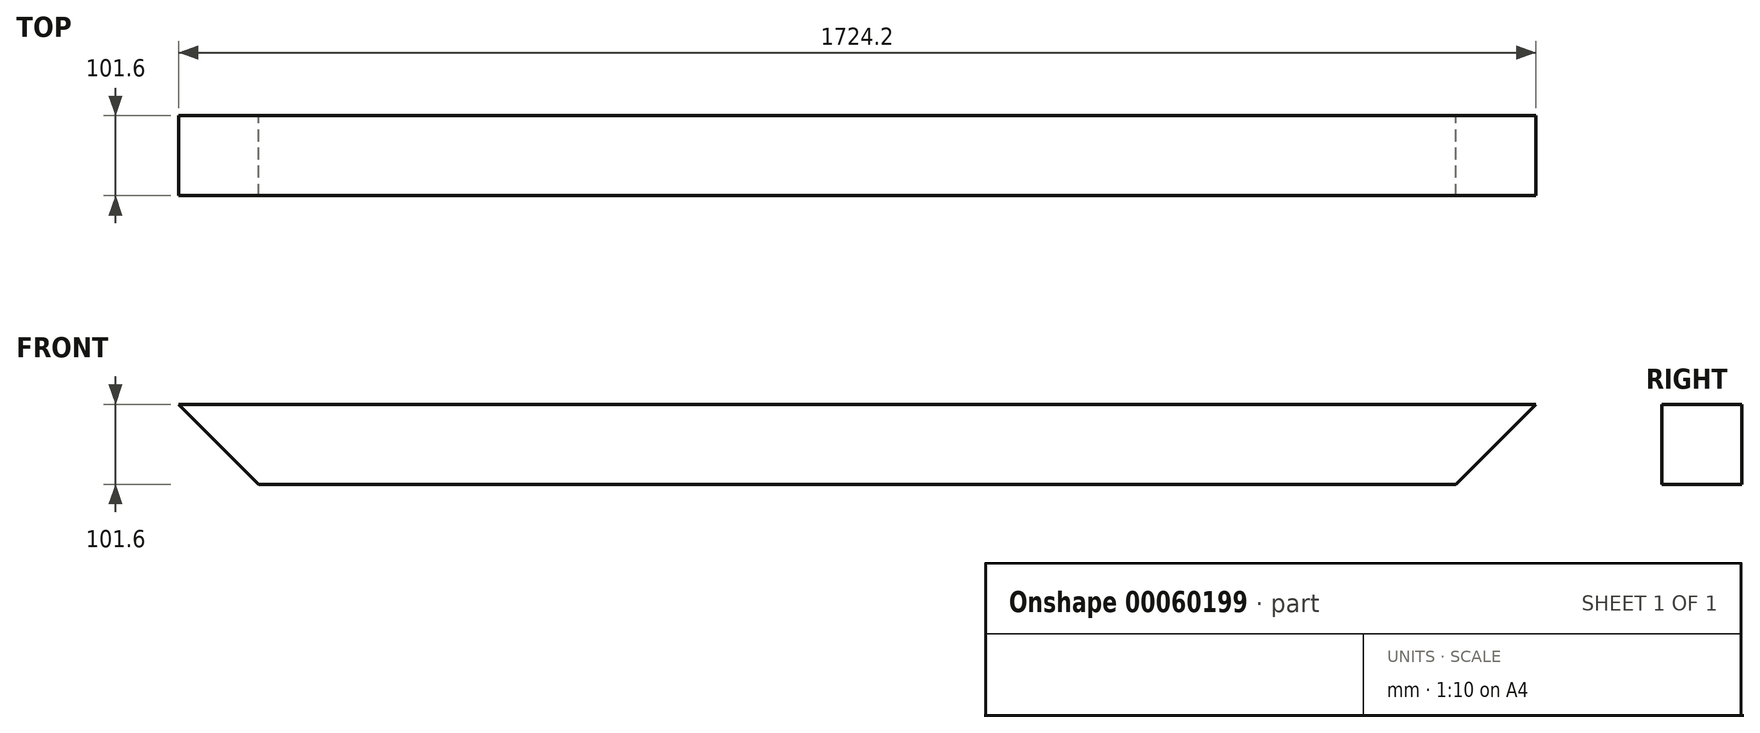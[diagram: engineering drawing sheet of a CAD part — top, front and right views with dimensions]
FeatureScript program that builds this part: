
annotation { "Feature Type Name" : "Feature", "Feature Type Description" : "" }
export const myFeature = defineFeature(function(context is Context, id is Id, definition is map)
    precondition{}
    {
        {
            var Q0;
            Q0=qCreatedBy(makeId("Front.planeOp"),FACE);
            var sketch = newSketch(context, id + "F0", { "sketchPlane" : qUnion([Q0])});
            skLineSegment(sketch, "E0.rect.bottom", {"start": v(862.1, 50.8) * mm, "end": v(-862.1, 50.8) * mm});
            skLineSegment(sketch, "E0.rect.top", {"start": v(862.1, -50.8) * mm, "end": v(-862.1, -50.8) * mm});
            skLineSegment(sketch, "E0.rect.left", {"start": v(862.1, 50.8) * mm, "end": v(862.1, -50.8) * mm});
            skLineSegment(sketch, "E0.rect.right", {"start": v(-862.1, 50.8) * mm, "end": v(-862.1, -50.8) * mm});
            skPoint(sketch, "E0.rect.middle", {"position": v(0, 0) * mm});
            skLineSegment(sketch, "E1", {"start": v(-862.1, 50.8) * mm, "end": v(0, -811.3) * mm});
            skLineSegment(sketch, "E2", {"start": v(0, -811.3) * mm, "end": v(862.1, 50.8) * mm});
            skSolve(sketch);
        }
        {
            var Q0;
            {var subQ0=sQuery(id+"F0.wireOp",EDGE,"E0.rect.bottom");Q0=makeQuery(id+"F0.imprint","IMPRINT",FACE,{"disambiguationData":[TD([[makeQuery(id+"F0.imprint","IMPRINT",EDGE,{"derivedFrom":subQ0}),1.0]])]});}
            extrude(context, id + "F1", {"entities" : qUnion([Q0]), "depth" : 101.6 * mm});
        }
    });
